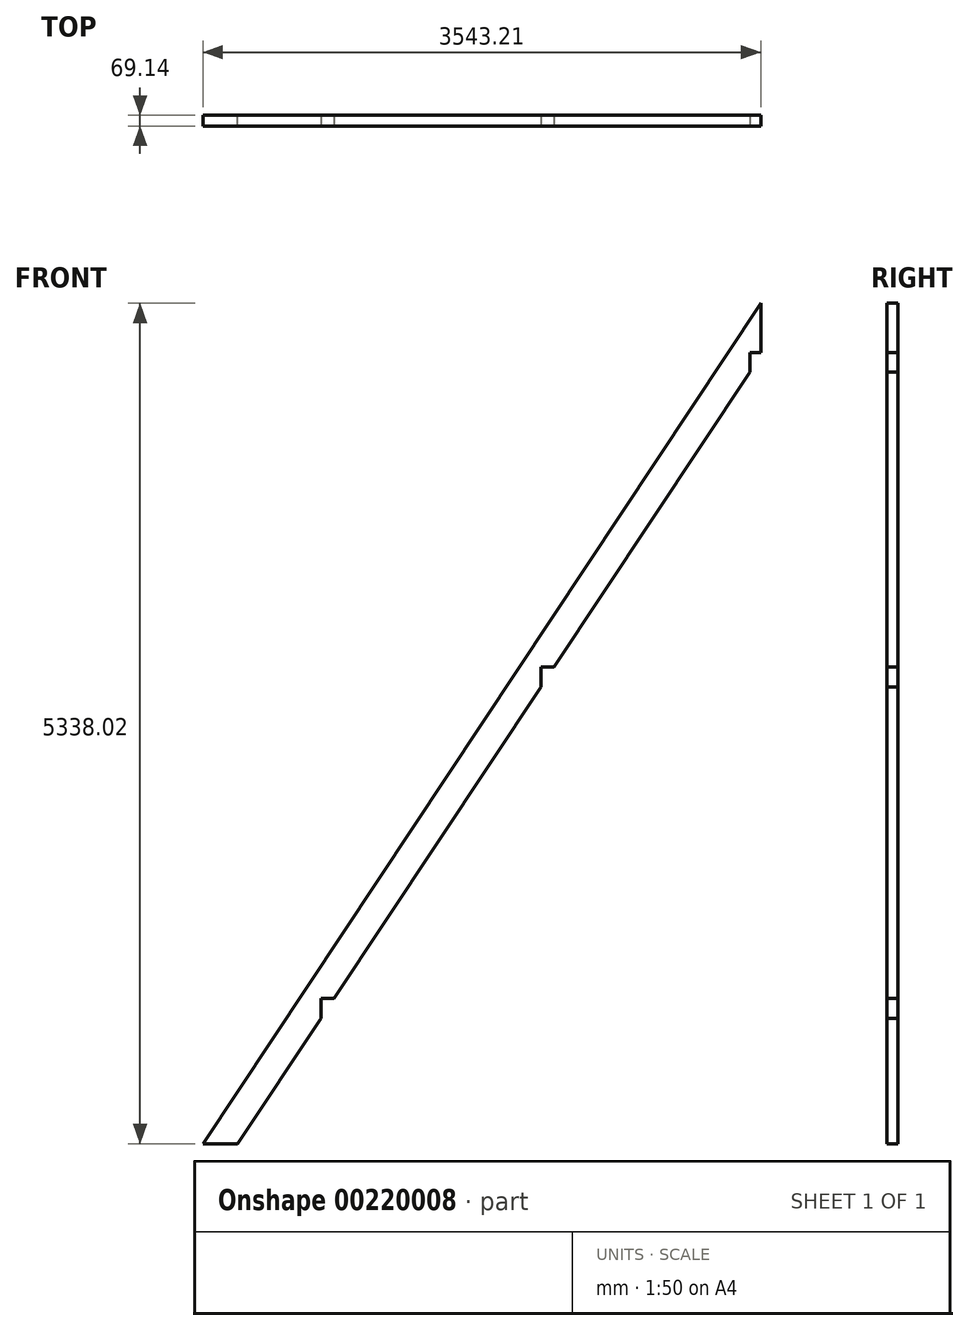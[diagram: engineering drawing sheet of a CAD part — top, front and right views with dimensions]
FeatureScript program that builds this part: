
annotation { "Feature Type Name" : "Feature", "Feature Type Description" : "" }
export const myFeature = defineFeature(function(context is Context, id is Id, definition is map)
    precondition{}
    {
        {
            var Q0;
            Q0=qCreatedBy(makeId("Front.planeOp"),FACE);
            var sketch = newSketch(context, id + "F0", { "sketchPlane" : qUnion([Q0])});
            skLineSegment(sketch, "E0", {"start": v(0, 0) * mm, "end": v(3543.21, 5338.02) * mm});
            skLineSegment(sketch, "E1", {"start": v(3543.21, 5338.02) * mm, "end": v(3543.21, 5005.03) * mm});
            skLineSegment(sketch, "E2", {"start": v(3543.21, 5005.03) * mm, "end": v(221.03, 0) * mm});
            skLineSegment(sketch, "E3", {"start": v(221.03, 0) * mm, "end": v(0, 0) * mm});
            skSolve(sketch);
        }
        {
            var Q0;
            Q0=makeQuery(id+"F0.imprint","IMPRINT",FACE,{"disambiguationData":[TD([[makeQuery(id+"F0.imprint","IMPRINT",EDGE,{"derivedFrom":sQuery(id+"F0.wireOp",EDGE,"E0")}),-1.0]])]});
            extrude(context, id + "F1", {"entities" : qUnion([Q0]), "depth" : 69.14 * mm});
        }
        {
            var Q0;
            Q0=makeQuery(id+"F1.opExtrude","CAP_FACE",FACE,{"disambiguationData":[OSD([sQuery(id+"F0.wireOp",EDGE,"E0"),sQuery(id+"F0.wireOp",EDGE,"E1"),sQuery(id+"F0.wireOp",EDGE,"E2"),sQuery(id+"F0.wireOp",EDGE,"E3")])],"isStart":false});
            var sketch = newSketch(context, id + "F2", { "sketchPlane" : qUnion([Q0])});
            skLineSegment(sketch, "E4.bottom", {"start": v(3473.36, 5026.1) * mm, "end": v(3613.06, 5026.1) * mm});
            skLineSegment(sketch, "E4.top", {"start": v(3473.36, 4886.4) * mm, "end": v(3613.06, 4886.4) * mm});
            skLineSegment(sketch, "E4.left", {"start": v(3473.36, 5026.1) * mm, "end": v(3473.36, 4886.4) * mm});
            skLineSegment(sketch, "E4.right", {"start": v(3613.06, 5026.1) * mm, "end": v(3613.06, 4886.4) * mm});
            skLineSegment(sketch, "E5.bottom", {"start": v(2146.21, 3026.69) * mm, "end": v(2285.91, 3026.69) * mm});
            skLineSegment(sketch, "E5.top", {"start": v(2146.21, 2886.99) * mm, "end": v(2285.91, 2886.99) * mm});
            skLineSegment(sketch, "E5.left", {"start": v(2146.21, 3026.69) * mm, "end": v(2146.21, 2886.99) * mm});
            skLineSegment(sketch, "E5.right", {"start": v(2285.91, 3026.69) * mm, "end": v(2285.91, 2886.99) * mm});
            skLineSegment(sketch, "E6.bottom", {"start": v(749.21, 922.04) * mm, "end": v(888.91, 922.04) * mm});
            skLineSegment(sketch, "E6.top", {"start": v(749.21, 782.34) * mm, "end": v(888.91, 782.34) * mm});
            skLineSegment(sketch, "E6.left", {"start": v(749.21, 922.04) * mm, "end": v(749.21, 782.34) * mm});
            skLineSegment(sketch, "E6.right", {"start": v(888.91, 922.04) * mm, "end": v(888.91, 782.34) * mm});
            skLineSegment(sketch, "E7", {"start": v(3473.36, 5026.1) * mm, "end": v(175.74, 58.07) * mm, "construction": true});
            skSolve(sketch);
        }
        {
            var Q0;
            {var subQ0=sQuery(id+"F2.wireOp",EDGE,"E4.left");var subQ1=sQuery(id+"F2.wireOp",EDGE,"E4.bottom");var subQ2=makeQuery(id+"F2.imprint","INTERSECT",VERTEX,{"derivedFrom":[subQ1,subQ0]});Q0=makeQuery(id+"F2.imprint","IMPRINT",FACE,{"disambiguationData":[TD([[makeQuery(id+"F2.imprint","IMPRINT",EDGE,{"disambiguationData":[TD([[subQ2,-1.0]])],"derivedFrom":subQ1}),-1.0]])]});}
            var Q1;
            {var subQ0=sQuery(id+"F2.wireOp",EDGE,"E5.left");var subQ1=sQuery(id+"F2.wireOp",EDGE,"E5.bottom");var subQ2=makeQuery(id+"F2.imprint","INTERSECT",VERTEX,{"derivedFrom":[subQ1,subQ0]});Q1=makeQuery(id+"F2.imprint","IMPRINT",FACE,{"disambiguationData":[TD([[makeQuery(id+"F2.imprint","IMPRINT",EDGE,{"disambiguationData":[TD([[subQ2,-1.0]])],"derivedFrom":subQ1}),-1.0]])]});}
            var Q2;
            {var subQ0=sQuery(id+"F2.wireOp",EDGE,"E6.left");var subQ1=sQuery(id+"F2.wireOp",EDGE,"E6.bottom");var subQ2=makeQuery(id+"F2.imprint","INTERSECT",VERTEX,{"derivedFrom":[subQ1,subQ0]});Q2=makeQuery(id+"F2.imprint","IMPRINT",FACE,{"disambiguationData":[TD([[makeQuery(id+"F2.imprint","IMPRINT",EDGE,{"disambiguationData":[TD([[subQ2,-1.0]])],"derivedFrom":subQ1}),-1.0]])]});}
            extrude(context, id + "F3", {"entities" : qUnion([Q0, Q1, Q2]), "operationType" : NewBodyOperationType.REMOVE, "endBound" : BoundingType.THROUGH_ALL, "oppositeDirection" : true, "depth" : 25.4 * mm});
        }
    });
